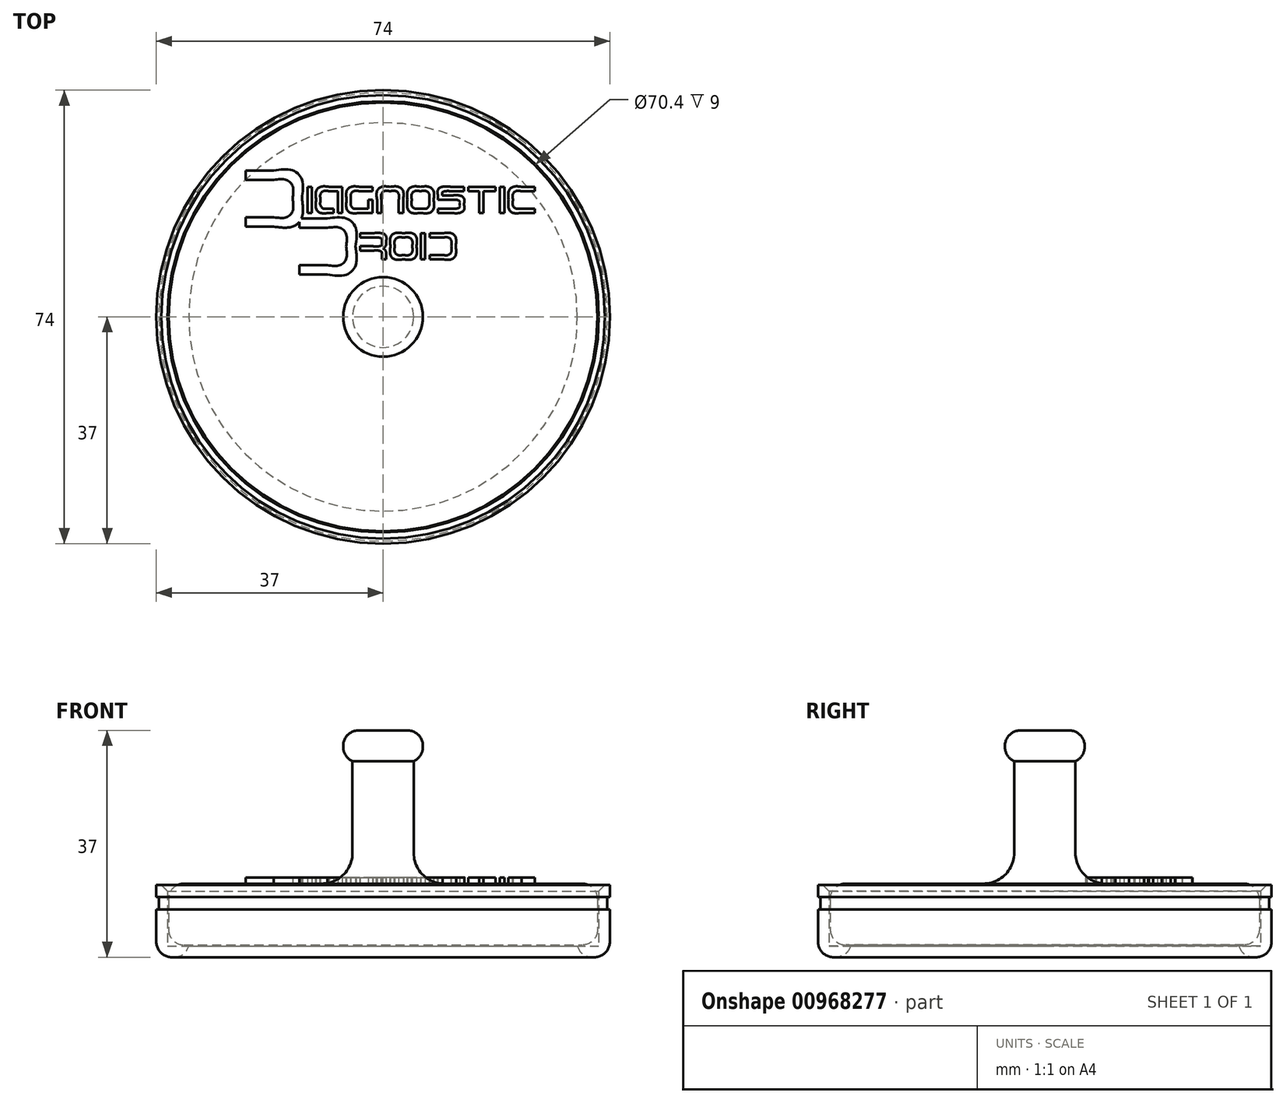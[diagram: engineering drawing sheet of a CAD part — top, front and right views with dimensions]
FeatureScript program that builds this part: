
annotation { "Feature Type Name" : "Feature", "Feature Type Description" : "" }
export const myFeature = defineFeature(function(context is Context, id is Id, definition is map)
    precondition{}
    {
        {
            var Q0;
            Q0=qCreatedBy(makeId("Front.planeOp"),FACE);
            var sketch = newSketch(context, id + "F0", { "sketchPlane" : qUnion([Q0])});
            skLineSegment(sketch, "E0.bottom", {"start": v(0, 0) * mm, "end": v(-35, 0) * mm});
            skLineSegment(sketch, "E0.top", {"start": v(0, 10) * mm, "end": v(-35, 10) * mm});
            skLineSegment(sketch, "E0.left", {"start": v(0, 0) * mm, "end": v(0, 10) * mm});
            skLineSegment(sketch, "E0.right", {"start": v(-35, 0) * mm, "end": v(-35, 6.5) * mm});
            skPoint(sketch, "E1.oppositeSnap0", {"position": v(-35, 5) * mm});
            skLineSegment(sketch, "E2.trimOffspring", {"start": v(-35, 3.5) * mm, "end": v(-35, 10) * mm});
            skLineSegment(sketch, "E3", {"start": v(-35, 6.5) * mm, "end": v(-35, 3.5) * mm});
            skPoint(sketch, "E1.top.end.orphan", {"position": v(-33.5, 6.5) * mm});
            skLineSegment(sketch, "E4.0", {"start": v(-37, -2) * mm, "end": v(-37, 9.8) * mm});
            skLineSegment(sketch, "E4.1", {"start": v(-31.7, -2) * mm, "end": v(-37, -2) * mm});
            skLineSegment(sketch, "E5.0", {"start": v(-35.2, -0.2) * mm, "end": v(-35.2, 9.8) * mm});
            skLineSegment(sketch, "E5.1", {"start": v(-31.7, -0.2) * mm, "end": v(-35.2, -0.2) * mm});
            skLineSegment(sketch, "E6", {"start": v(-35.2, 9.8) * mm, "end": v(-37, 9.8) * mm});
            skLineSegment(sketch, "E7", {"start": v(-31.7, -0.2) * mm, "end": v(-31.7, -2) * mm});
            skLineSegment(sketch, "E8.bottom", {"start": v(-37, 7.8) * mm, "end": v(-36.6, 7.8) * mm});
            skLineSegment(sketch, "E8.top", {"start": v(-37, 5.8) * mm, "end": v(-36.6, 5.8) * mm});
            skLineSegment(sketch, "E8.left", {"start": v(-37, 7.8) * mm, "end": v(-37, 5.8) * mm});
            skLineSegment(sketch, "E8.right", {"start": v(-36.6, 7.8) * mm, "end": v(-36.6, 5.8) * mm});
            skSolve(sketch);
        }
        {
            var Q0;
            Q0=makeQuery(id+"F0.imprint","IMPRINT",FACE,{"disambiguationData":[TD([[makeQuery(id+"F0.imprint","IMPRINT",EDGE,{"derivedFrom":sQuery(id+"F0.wireOp",EDGE,"E0.bottom")}),-1.0]])]});
            var Q1;
            Q1=makeQuery(id+"F0.imprint","IMPRINT",FACE,{"disambiguationData":[TD([[makeQuery(id+"F0.imprint","IMPRINT",EDGE,{"derivedFrom":sQuery(id+"F0.wireOp",EDGE,"E4.0")}),-1.0]])]});
            var Q2;
            Q2=sQuery(id+"F0.wireOp",EDGE,"E0.left");
            revolve(context, id + "F1", {"entities" : qUnion([Q0, Q1]), "axis" : qUnion([Q2]), "revolveType" : RevolveType.FULL});
        }
        {
            var Q0;
            Q0=makeQuery(id+"F1.opRevolve","SWEPT_FACE",FACE,{"disambiguationData":[OSD([sQuery(id+"F0.wireOp",EDGE,"E0.top")])]});
            var sketch = newSketch(context, id + "F2", { "sketchPlane" : qUnion([Q0])});
            skLineSegment(sketch, "E9", {"start": v(-11.63, 21.23) * mm, "end": v(-11.63, 16.97) * mm});
            skLineSegment(sketch, "E10", {"start": v(-11.63, 16.97) * mm, "end": v(-12.34, 16.97) * mm});
            skLineSegment(sketch, "E11", {"start": v(-12.34, 16.97) * mm, "end": v(-12.34, 21.23) * mm});
            skLineSegment(sketch, "E12", {"start": v(-12.34, 21.23) * mm, "end": v(-11.63, 21.23) * mm});
            skFitSpline(sketch, "E13", {"points": [v(-8.8, 20.52) * mm, v(-9.74, 20.52) * mm, v(-10.21, 20.04) * mm, v(-10.21, 19.1) * mm]});
            skFitSpline(sketch, "E14", {"points": [v(-10.21, 19.1) * mm, v(-10.21, 18.15) * mm, v(-9.74, 17.68) * mm, v(-8.8, 17.68) * mm]});
            skLineSegment(sketch, "E15", {"start": v(-6.67, 21.23) * mm, "end": v(-6.67, 16.97) * mm});
            skLineSegment(sketch, "E16", {"start": v(-6.67, 16.97) * mm, "end": v(-7.37, 16.97) * mm});
            skLineSegment(sketch, "E17", {"start": v(-7.37, 16.97) * mm, "end": v(-7.37, 20.52) * mm});
            skLineSegment(sketch, "E18", {"start": v(-7.37, 20.52) * mm, "end": v(-8.8, 20.52) * mm});
            skFitSpline(sketch, "E19", {"points": [v(-8.8, 16.97) * mm, v(-10.21, 16.97) * mm, v(-10.92, 17.68) * mm, v(-10.92, 19.1) * mm]});
            skFitSpline(sketch, "E20", {"points": [v(-10.92, 19.1) * mm, v(-10.92, 20.52) * mm, v(-10.21, 21.23) * mm, v(-8.8, 21.23) * mm]});
            skLineSegment(sketch, "E21", {"start": v(-8.8, 17.68) * mm, "end": v(-8.08, 17.68) * mm});
            skLineSegment(sketch, "E22", {"start": v(-8.08, 17.68) * mm, "end": v(-8.08, 16.97) * mm});
            skLineSegment(sketch, "E23", {"start": v(-8.08, 16.97) * mm, "end": v(-8.8, 16.97) * mm});
            skLineSegment(sketch, "E24", {"start": v(-8.8, 21.23) * mm, "end": v(-6.67, 21.23) * mm});
            skFitSpline(sketch, "E25", {"points": [v(-3.83, 16.97) * mm, v(-5.25, 16.97) * mm, v(-5.96, 17.68) * mm, v(-5.96, 19.1) * mm]});
            skFitSpline(sketch, "E26", {"points": [v(-5.96, 19.1) * mm, v(-5.96, 20.52) * mm, v(-5.25, 21.23) * mm, v(-3.83, 21.23) * mm]});
            skLineSegment(sketch, "E27", {"start": v(-1.7, 19.1) * mm, "end": v(-1.7, 16.97) * mm});
            skLineSegment(sketch, "E28", {"start": v(-1.7, 16.97) * mm, "end": v(-3.83, 16.97) * mm});
            skFitSpline(sketch, "E29", {"points": [v(-3.83, 20.52) * mm, v(-4.77, 20.52) * mm, v(-5.25, 20.04) * mm, v(-5.25, 19.1) * mm]});
            skFitSpline(sketch, "E30", {"points": [v(-5.25, 19.1) * mm, v(-5.25, 18.15) * mm, v(-4.77, 17.68) * mm, v(-3.83, 17.68) * mm]});
            skLineSegment(sketch, "E31", {"start": v(-3.83, 21.23) * mm, "end": v(-1.7, 21.23) * mm});
            skLineSegment(sketch, "E32", {"start": v(-1.7, 21.23) * mm, "end": v(-1.7, 20.52) * mm});
            skLineSegment(sketch, "E33", {"start": v(-1.7, 20.52) * mm, "end": v(-3.83, 20.52) * mm});
            skLineSegment(sketch, "E34", {"start": v(-3.83, 17.68) * mm, "end": v(-2.4, 17.68) * mm});
            skLineSegment(sketch, "E35", {"start": v(-2.4, 17.68) * mm, "end": v(-2.4, 19.1) * mm});
            skLineSegment(sketch, "E36", {"start": v(-2.4, 19.1) * mm, "end": v(-1.7, 19.1) * mm});
            skFitSpline(sketch, "E37", {"points": [v(-0.99, 19.1) * mm, v(-0.99, 20.52) * mm, v(-0.28, 21.23) * mm, v(1.14, 21.23) * mm]});
            skFitSpline(sketch, "E38", {"points": [v(1.14, 21.23) * mm, v(2.56, 21.23) * mm, v(3.27, 20.52) * mm, v(3.27, 19.1) * mm]});
            skLineSegment(sketch, "E39", {"start": v(-0.28, 19.1) * mm, "end": v(-0.28, 16.97) * mm});
            skLineSegment(sketch, "E40", {"start": v(-0.28, 16.97) * mm, "end": v(-0.99, 16.97) * mm});
            skLineSegment(sketch, "E41", {"start": v(-0.99, 16.97) * mm, "end": v(-0.99, 19.1) * mm});
            skFitSpline(sketch, "E42", {"points": [v(2.56, 19.1) * mm, v(2.56, 20.04) * mm, v(2.09, 20.52) * mm, v(1.14, 20.52) * mm]});
            skFitSpline(sketch, "E43", {"points": [v(1.14, 20.52) * mm, v(0.2, 20.52) * mm, v(-0.28, 20.04) * mm, v(-0.28, 19.1) * mm]});
            skLineSegment(sketch, "E44", {"start": v(3.27, 19.1) * mm, "end": v(3.27, 16.97) * mm});
            skLineSegment(sketch, "E45", {"start": v(3.27, 16.97) * mm, "end": v(2.56, 16.97) * mm});
            skLineSegment(sketch, "E46", {"start": v(2.56, 16.97) * mm, "end": v(2.56, 19.1) * mm});
            skFitSpline(sketch, "E47", {"points": [v(3.98, 19.1) * mm, v(3.98, 20.52) * mm, v(4.7, 21.23) * mm, v(6.11, 21.23) * mm]});
            skFitSpline(sketch, "E48", {"points": [v(6.11, 21.23) * mm, v(7.53, 21.23) * mm, v(8.24, 20.52) * mm, v(8.24, 19.1) * mm]});
            skFitSpline(sketch, "E49", {"points": [v(8.24, 19.1) * mm, v(8.24, 17.68) * mm, v(7.53, 16.97) * mm, v(6.11, 16.97) * mm]});
            skFitSpline(sketch, "E50", {"points": [v(6.11, 16.97) * mm, v(4.7, 16.97) * mm, v(3.98, 17.68) * mm, v(3.98, 19.1) * mm]});
            skFitSpline(sketch, "E51", {"points": [v(4.7, 19.1) * mm, v(4.7, 18.15) * mm, v(5.16, 17.68) * mm, v(6.11, 17.68) * mm]});
            skFitSpline(sketch, "E52", {"points": [v(6.11, 17.68) * mm, v(7.06, 17.68) * mm, v(7.53, 18.15) * mm, v(7.53, 19.1) * mm]});
            skFitSpline(sketch, "E53", {"points": [v(7.53, 19.1) * mm, v(7.53, 20.04) * mm, v(7.06, 20.52) * mm, v(6.11, 20.52) * mm]});
            skFitSpline(sketch, "E54", {"points": [v(6.11, 20.52) * mm, v(5.16, 20.52) * mm, v(4.7, 20.04) * mm, v(4.7, 19.1) * mm]});
            skFitSpline(sketch, "E55", {"points": [v(8.95, 19.8) * mm, v(8.95, 20.75) * mm, v(9.66, 21.23) * mm, v(11.08, 21.23) * mm]});
            skFitSpline(sketch, "E56", {"points": [v(11.08, 20.52) * mm, v(10.13, 20.52) * mm, v(9.66, 20.28) * mm, v(9.66, 19.8) * mm]});
            skLineSegment(sketch, "E57", {"start": v(11.08, 21.23) * mm, "end": v(13.2, 21.23) * mm});
            skLineSegment(sketch, "E58", {"start": v(13.2, 21.23) * mm, "end": v(13.2, 20.52) * mm});
            skLineSegment(sketch, "E59", {"start": v(13.2, 20.52) * mm, "end": v(11.08, 20.52) * mm});
            skFitSpline(sketch, "E60", {"points": [v(11.08, 19.8) * mm, v(12.5, 19.8) * mm, v(13.2, 19.33) * mm, v(13.2, 18.39) * mm]});
            skFitSpline(sketch, "E61", {"points": [v(13.2, 18.39) * mm, v(13.2, 17.44) * mm, v(12.5, 16.97) * mm, v(11.08, 16.97) * mm]});
            skLineSegment(sketch, "E62", {"start": v(9.66, 19.8) * mm, "end": v(11.08, 19.8) * mm});
            skFitSpline(sketch, "E63", {"points": [v(11.08, 17.68) * mm, v(12.03, 17.68) * mm, v(12.5, 17.91) * mm, v(12.5, 18.39) * mm]});
            skFitSpline(sketch, "E64", {"points": [v(12.5, 18.39) * mm, v(12.5, 18.86) * mm, v(12.03, 19.1) * mm, v(11.08, 19.1) * mm]});
            skLineSegment(sketch, "E65", {"start": v(11.08, 16.97) * mm, "end": v(8.95, 16.97) * mm});
            skLineSegment(sketch, "E66", {"start": v(8.95, 16.97) * mm, "end": v(8.95, 17.68) * mm});
            skLineSegment(sketch, "E67", {"start": v(8.95, 17.68) * mm, "end": v(11.08, 17.68) * mm});
            skLineSegment(sketch, "E68", {"start": v(11.08, 19.1) * mm, "end": v(8.95, 19.1) * mm});
            skLineSegment(sketch, "E69", {"start": v(8.95, 19.1) * mm, "end": v(8.95, 19.8) * mm});
            skLineSegment(sketch, "E70", {"start": v(13.92, 21.23) * mm, "end": v(18.36, 21.23) * mm});
            skLineSegment(sketch, "E71", {"start": v(18.36, 21.23) * mm, "end": v(18.36, 20.52) * mm});
            skLineSegment(sketch, "E72", {"start": v(18.36, 20.52) * mm, "end": v(16.4, 20.52) * mm});
            skLineSegment(sketch, "E73", {"start": v(16.4, 20.52) * mm, "end": v(16.4, 16.97) * mm});
            skLineSegment(sketch, "E74", {"start": v(16.4, 16.97) * mm, "end": v(15.7, 16.97) * mm});
            skLineSegment(sketch, "E75", {"start": v(15.7, 16.97) * mm, "end": v(15.7, 20.52) * mm});
            skLineSegment(sketch, "E76", {"start": v(15.7, 20.52) * mm, "end": v(13.92, 20.52) * mm});
            skLineSegment(sketch, "E77", {"start": v(13.92, 20.52) * mm, "end": v(13.92, 21.23) * mm});
            skFitSpline(sketch, "E78", {"points": [v(21.2, 19.1) * mm, v(21.2, 18.15) * mm, v(21.67, 17.68) * mm, v(22.62, 17.68) * mm]});
            skLineSegment(sketch, "E79", {"start": v(19.78, 21.23) * mm, "end": v(19.78, 16.97) * mm});
            skLineSegment(sketch, "E80", {"start": v(19.78, 16.97) * mm, "end": v(19.07, 16.97) * mm});
            skLineSegment(sketch, "E81", {"start": v(19.07, 16.97) * mm, "end": v(19.07, 21.23) * mm});
            skLineSegment(sketch, "E82", {"start": v(19.07, 21.23) * mm, "end": v(19.78, 21.23) * mm});
            skFitSpline(sketch, "E83", {"points": [v(22.62, 16.97) * mm, v(21.2, 16.97) * mm, v(20.5, 17.68) * mm, v(20.5, 19.1) * mm]});
            skFitSpline(sketch, "E84", {"points": [v(20.5, 19.1) * mm, v(20.5, 20.52) * mm, v(21.2, 21.23) * mm, v(22.62, 21.23) * mm]});
            skLineSegment(sketch, "E85", {"start": v(22.62, 17.68) * mm, "end": v(24.75, 17.68) * mm});
            skLineSegment(sketch, "E86", {"start": v(24.75, 17.68) * mm, "end": v(24.75, 16.97) * mm});
            skLineSegment(sketch, "E87", {"start": v(24.75, 16.97) * mm, "end": v(22.62, 16.97) * mm});
            skFitSpline(sketch, "E88", {"points": [v(22.62, 20.52) * mm, v(21.67, 20.52) * mm, v(21.2, 20.04) * mm, v(21.2, 19.1) * mm]});
            skLineSegment(sketch, "E89", {"start": v(22.62, 21.23) * mm, "end": v(24.75, 21.23) * mm});
            skLineSegment(sketch, "E90", {"start": v(24.75, 21.23) * mm, "end": v(24.75, 20.52) * mm});
            skLineSegment(sketch, "E91", {"start": v(24.75, 20.52) * mm, "end": v(22.62, 20.52) * mm});
            skFitSpline(sketch, "E92", {"points": [v(-1.64, 11.52) * mm, v(-0.7, 11.52) * mm, v(-0.22, 11.76) * mm, v(-0.22, 12.23) * mm]});
            skFitSpline(sketch, "E93", {"points": [v(-0.22, 12.23) * mm, v(-0.22, 12.7) * mm, v(-0.7, 12.94) * mm, v(-1.64, 12.94) * mm]});
            skFitSpline(sketch, "E94", {"points": [v(-1.64, 13.65) * mm, v(-0.22, 13.65) * mm, v(0.5, 13.18) * mm, v(0.5, 12.23) * mm]});
            skFitSpline(sketch, "E95", {"points": [v(0.5, 12.23) * mm, v(0.5, 11.76) * mm, v(0.32, 11.4) * mm, v(-0.04, 11.17) * mm]});
            skFitSpline(sketch, "E96", {"points": [v(-0.04, 11.17) * mm, v(0.32, 10.93) * mm, v(0.5, 10.58) * mm, v(0.5, 10.1) * mm]});
            skLineSegment(sketch, "E97", {"start": v(-1.64, 12.94) * mm, "end": v(-3.77, 12.94) * mm});
            skLineSegment(sketch, "E98", {"start": v(-3.77, 12.94) * mm, "end": v(-3.77, 13.65) * mm});
            skLineSegment(sketch, "E99", {"start": v(-3.77, 13.65) * mm, "end": v(-1.64, 13.65) * mm});
            skFitSpline(sketch, "E100", {"points": [v(-0.22, 10.1) * mm, v(-0.22, 10.58) * mm, v(-0.7, 10.81) * mm, v(-1.64, 10.81) * mm]});
            skLineSegment(sketch, "E101", {"start": v(0.5, 10.1) * mm, "end": v(0.5, 9.4) * mm});
            skLineSegment(sketch, "E102", {"start": v(0.5, 9.4) * mm, "end": v(-0.22, 9.4) * mm});
            skLineSegment(sketch, "E103", {"start": v(-0.22, 9.4) * mm, "end": v(-0.22, 10.1) * mm});
            skFitSpline(sketch, "E104", {"points": [v(1.2, 11.52) * mm, v(1.2, 12.94) * mm, v(1.91, 13.65) * mm, v(3.33, 13.65) * mm]});
            skFitSpline(sketch, "E105", {"points": [v(3.33, 13.65) * mm, v(4.75, 13.65) * mm, v(5.46, 12.94) * mm, v(5.46, 11.52) * mm]});
            skFitSpline(sketch, "E106", {"points": [v(5.46, 11.52) * mm, v(5.46, 10.1) * mm, v(4.75, 9.4) * mm, v(3.33, 9.4) * mm]});
            skFitSpline(sketch, "E107", {"points": [v(3.33, 9.4) * mm, v(1.91, 9.4) * mm, v(1.2, 10.1) * mm, v(1.2, 11.52) * mm]});
            skLineSegment(sketch, "E108", {"start": v(-1.64, 10.81) * mm, "end": v(-3.77, 10.81) * mm});
            skLineSegment(sketch, "E109", {"start": v(-3.77, 10.81) * mm, "end": v(-3.77, 11.52) * mm});
            skLineSegment(sketch, "E110", {"start": v(-3.77, 11.52) * mm, "end": v(-1.64, 11.52) * mm});
            skFitSpline(sketch, "E111", {"points": [v(1.91, 11.52) * mm, v(1.91, 10.58) * mm, v(2.39, 10.1) * mm, v(3.33, 10.1) * mm]});
            skFitSpline(sketch, "E112", {"points": [v(3.33, 10.1) * mm, v(4.28, 10.1) * mm, v(4.75, 10.58) * mm, v(4.75, 11.52) * mm]});
            skFitSpline(sketch, "E113", {"points": [v(4.75, 11.52) * mm, v(4.75, 12.47) * mm, v(4.28, 12.94) * mm, v(3.33, 12.94) * mm]});
            skFitSpline(sketch, "E114", {"points": [v(3.33, 12.94) * mm, v(2.39, 12.94) * mm, v(1.91, 12.47) * mm, v(1.91, 11.52) * mm]});
            skLineSegment(sketch, "E115", {"start": v(6.88, 13.65) * mm, "end": v(6.88, 9.4) * mm});
            skLineSegment(sketch, "E116", {"start": v(6.88, 9.4) * mm, "end": v(6.17, 9.4) * mm});
            skLineSegment(sketch, "E117", {"start": v(6.17, 9.4) * mm, "end": v(6.17, 13.65) * mm});
            skLineSegment(sketch, "E118", {"start": v(6.17, 13.65) * mm, "end": v(6.88, 13.65) * mm});
            skFitSpline(sketch, "E119", {"points": [v(9.72, 13.65) * mm, v(11.14, 13.65) * mm, v(11.85, 12.94) * mm, v(11.85, 11.52) * mm]});
            skFitSpline(sketch, "E120", {"points": [v(11.85, 11.52) * mm, v(11.85, 10.1) * mm, v(11.14, 9.4) * mm, v(9.72, 9.4) * mm]});
            skLineSegment(sketch, "E121", {"start": v(9.72, 12.94) * mm, "end": v(7.6, 12.94) * mm});
            skLineSegment(sketch, "E122", {"start": v(7.6, 12.94) * mm, "end": v(7.6, 13.65) * mm});
            skLineSegment(sketch, "E123", {"start": v(7.6, 13.65) * mm, "end": v(9.72, 13.65) * mm});
            skFitSpline(sketch, "E124", {"points": [v(9.72, 10.1) * mm, v(10.67, 10.1) * mm, v(11.14, 10.58) * mm, v(11.14, 11.52) * mm]});
            skFitSpline(sketch, "E125", {"points": [v(11.14, 11.52) * mm, v(11.14, 12.47) * mm, v(10.67, 12.94) * mm, v(9.72, 12.94) * mm]});
            skLineSegment(sketch, "E126", {"start": v(9.72, 9.4) * mm, "end": v(7.6, 9.4) * mm});
            skLineSegment(sketch, "E127", {"start": v(7.6, 9.4) * mm, "end": v(7.6, 10.1) * mm});
            skLineSegment(sketch, "E128", {"start": v(7.6, 10.1) * mm, "end": v(9.72, 10.1) * mm});
            skFitSpline(sketch, "E129", {"points": [v(-17.82, 23.9) * mm, v(-14.77, 23.9) * mm, v(-13.24, 22.37) * mm, v(-13.24, 19.3) * mm]});
            skFitSpline(sketch, "E130", {"points": [v(-13.24, 19.3) * mm, v(-13.24, 16.25) * mm, v(-14.77, 14.72) * mm, v(-17.82, 14.72) * mm]});
            skLineSegment(sketch, "E131", {"start": v(-17.82, 22.37) * mm, "end": v(-22.4, 22.37) * mm});
            skLineSegment(sketch, "E132", {"start": v(-22.4, 22.37) * mm, "end": v(-22.4, 23.9) * mm});
            skLineSegment(sketch, "E133", {"start": v(-22.4, 23.9) * mm, "end": v(-17.82, 23.9) * mm});
            skFitSpline(sketch, "E134", {"points": [v(-17.82, 16.25) * mm, v(-15.79, 16.25) * mm, v(-14.77, 17.27) * mm, v(-14.77, 19.3) * mm]});
            skFitSpline(sketch, "E135", {"points": [v(-14.77, 19.3) * mm, v(-14.77, 21.35) * mm, v(-15.79, 22.37) * mm, v(-17.82, 22.37) * mm]});
            skLineSegment(sketch, "E136", {"start": v(-17.82, 14.72) * mm, "end": v(-22.4, 14.72) * mm});
            skLineSegment(sketch, "E137", {"start": v(-22.4, 14.72) * mm, "end": v(-22.4, 16.25) * mm});
            skLineSegment(sketch, "E138", {"start": v(-22.4, 16.25) * mm, "end": v(-17.82, 16.25) * mm});
            skFitSpline(sketch, "E139", {"points": [v(-9.08, 16.07) * mm, v(-6.02, 16.07) * mm, v(-4.5, 14.54) * mm, v(-4.5, 11.48) * mm]});
            skFitSpline(sketch, "E140", {"points": [v(-4.5, 11.48) * mm, v(-4.5, 8.42) * mm, v(-6.02, 6.9) * mm, v(-9.08, 6.9) * mm]});
            skLineSegment(sketch, "E141", {"start": v(-9.08, 14.54) * mm, "end": v(-13.66, 14.54) * mm});
            skLineSegment(sketch, "E142", {"start": v(-13.66, 14.54) * mm, "end": v(-13.66, 16.07) * mm});
            skLineSegment(sketch, "E143", {"start": v(-13.66, 16.07) * mm, "end": v(-9.08, 16.07) * mm});
            skFitSpline(sketch, "E144", {"points": [v(-9.08, 8.42) * mm, v(-7.04, 8.42) * mm, v(-6.02, 9.44) * mm, v(-6.02, 11.48) * mm]});
            skFitSpline(sketch, "E145", {"points": [v(-6.02, 11.48) * mm, v(-6.02, 13.52) * mm, v(-7.04, 14.54) * mm, v(-9.08, 14.54) * mm]});
            skLineSegment(sketch, "E146", {"start": v(-9.04, 6.9) * mm, "end": v(-13.66, 6.9) * mm});
            skLineSegment(sketch, "E147", {"start": v(-13.66, 8.42) * mm, "end": v(-9.04, 8.42) * mm});
            skLineSegment(sketch, "E148", {"start": v(-13.66, 8.42) * mm, "end": v(-13.66, 6.9) * mm});
            skSolve(sketch);
        }
        {
            var Q0;
            Q0=makeQuery(id+"F2.imprint","IMPRINT",FACE,{"disambiguationData":[TD([[makeQuery(id+"F2.imprint","IMPRINT",EDGE,{"derivedFrom":sQuery(id+"F2.wireOp",EDGE,"E139")}),-1.0]])]});
            var Q1;
            Q1=makeQuery(id+"F2.imprint","IMPRINT",FACE,{"disambiguationData":[TD([[makeQuery(id+"F2.imprint","IMPRINT",EDGE,{"derivedFrom":sQuery(id+"F2.wireOp",EDGE,"E92")}),-1.0]])]});
            var Q2;
            Q2=makeQuery(id+"F2.imprint","IMPRINT",FACE,{"disambiguationData":[TD([[makeQuery(id+"F2.imprint","IMPRINT",EDGE,{"derivedFrom":sQuery(id+"F2.wireOp",EDGE,"E104")}),-1.0]])]});
            var Q3;
            Q3=makeQuery(id+"F2.imprint","IMPRINT",FACE,{"disambiguationData":[TD([[makeQuery(id+"F2.imprint","IMPRINT",EDGE,{"derivedFrom":sQuery(id+"F2.wireOp",EDGE,"E119")}),-1.0]])]});
            var Q4;
            Q4=makeQuery(id+"F2.imprint","IMPRINT",FACE,{"disambiguationData":[TD([[makeQuery(id+"F2.imprint","IMPRINT",EDGE,{"derivedFrom":sQuery(id+"F2.wireOp",EDGE,"E115")}),-1.0]])]});
            var Q5;
            Q5=makeQuery(id+"F2.imprint","IMPRINT",FACE,{"disambiguationData":[TD([[makeQuery(id+"F2.imprint","IMPRINT",EDGE,{"derivedFrom":sQuery(id+"F2.wireOp",EDGE,"E37")}),-1.0]])]});
            var Q6;
            Q6=makeQuery(id+"F2.imprint","IMPRINT",FACE,{"disambiguationData":[TD([[makeQuery(id+"F2.imprint","IMPRINT",EDGE,{"derivedFrom":sQuery(id+"F2.wireOp",EDGE,"E25")}),-1.0]])]});
            var Q7;
            Q7=makeQuery(id+"F2.imprint","IMPRINT",FACE,{"disambiguationData":[TD([[makeQuery(id+"F2.imprint","IMPRINT",EDGE,{"derivedFrom":sQuery(id+"F2.wireOp",EDGE,"E13")}),-1.0]])]});
            var Q8;
            Q8=makeQuery(id+"F2.imprint","IMPRINT",FACE,{"disambiguationData":[TD([[makeQuery(id+"F2.imprint","IMPRINT",EDGE,{"derivedFrom":sQuery(id+"F2.wireOp",EDGE,"E9")}),-1.0]])]});
            var Q9;
            Q9=makeQuery(id+"F2.imprint","IMPRINT",FACE,{"disambiguationData":[TD([[makeQuery(id+"F2.imprint","IMPRINT",EDGE,{"derivedFrom":sQuery(id+"F2.wireOp",EDGE,"E129")}),-1.0]])]});
            var Q10;
            Q10=makeQuery(id+"F2.imprint","IMPRINT",FACE,{"disambiguationData":[TD([[makeQuery(id+"F2.imprint","IMPRINT",EDGE,{"derivedFrom":sQuery(id+"F2.wireOp",EDGE,"E47")}),-1.0]])]});
            var Q11;
            Q11=makeQuery(id+"F2.imprint","IMPRINT",FACE,{"disambiguationData":[TD([[makeQuery(id+"F2.imprint","IMPRINT",EDGE,{"derivedFrom":sQuery(id+"F2.wireOp",EDGE,"E55")}),-1.0]])]});
            var Q12;
            Q12=makeQuery(id+"F2.imprint","IMPRINT",FACE,{"disambiguationData":[TD([[makeQuery(id+"F2.imprint","IMPRINT",EDGE,{"derivedFrom":sQuery(id+"F2.wireOp",EDGE,"E70")}),-1.0]])]});
            var Q13;
            Q13=makeQuery(id+"F2.imprint","IMPRINT",FACE,{"disambiguationData":[TD([[makeQuery(id+"F2.imprint","IMPRINT",EDGE,{"derivedFrom":sQuery(id+"F2.wireOp",EDGE,"E79")}),-1.0]])]});
            var Q14;
            Q14=makeQuery(id+"F2.imprint","IMPRINT",FACE,{"disambiguationData":[TD([[makeQuery(id+"F2.imprint","IMPRINT",EDGE,{"derivedFrom":sQuery(id+"F2.wireOp",EDGE,"E78")}),-1.0]])]});
            var Q15;
            Q15=sQuery(id+"F2.wireOp",EDGE,"E99");
            var Q16;
            Q16=sQuery(id+"F2.wireOp",EDGE,"E115");
            var Q17;
            Q17=sQuery(id+"F2.wireOp",EDGE,"E131");
            var Q18;
            Q18=sQuery(id+"F2.wireOp",EDGE,"E147");
            var Q19;
            Q19=sQuery(id+"F2.wireOp",EDGE,"E51");
            var Q20;
            Q20=sQuery(id+"F2.wireOp",EDGE,"E67");
            var Q21;
            Q21=sQuery(id+"F2.wireOp",EDGE,"E83");
            var Q22;
            Q22=sQuery(id+"F2.wireOp",EDGE,"E114");
            var Q23;
            Q23=sQuery(id+"F2.wireOp",EDGE,"E130");
            var Q24;
            Q24=sQuery(id+"F2.wireOp",EDGE,"E146");
            var Q25;
            Q25=sQuery(id+"F2.wireOp",EDGE,"E50");
            var Q26;
            Q26=sQuery(id+"F2.wireOp",EDGE,"E20");
            var Q27;
            Q27=sQuery(id+"F2.wireOp",EDGE,"E19");
            var Q28;
            Q28=sQuery(id+"F2.wireOp",EDGE,"E17");
            var Q29;
            Q29=sQuery(id+"F2.wireOp",EDGE,"E15");
            var Q30;
            Q30=sQuery(id+"F2.wireOp",EDGE,"E14");
            var Q31;
            Q31=sQuery(id+"F2.wireOp",EDGE,"E13");
            var Q32;
            Q32=sQuery(id+"F2.wireOp",EDGE,"E11");
            var Q33;
            Q33=sQuery(id+"F2.wireOp",EDGE,"E9");
            var Q34;
            Q34=sQuery(id+"F2.wireOp",EDGE,"E97");
            var Q35;
            Q35=sQuery(id+"F2.wireOp",EDGE,"E113");
            var Q36;
            Q36=sQuery(id+"F2.wireOp",EDGE,"E129");
            var Q37;
            Q37=sQuery(id+"F2.wireOp",EDGE,"E145");
            var Q38;
            Q38=sQuery(id+"F2.wireOp",EDGE,"E33");
            var Q39;
            Q39=sQuery(id+"F2.wireOp",EDGE,"E49");
            var Q40;
            Q40=sQuery(id+"F2.wireOp",EDGE,"E65");
            var Q41;
            Q41=sQuery(id+"F2.wireOp",EDGE,"E81");
            var Q42;
            Q42=sQuery(id+"F2.wireOp",EDGE,"E112");
            var Q43;
            Q43=sQuery(id+"F2.wireOp",EDGE,"E128");
            var Q44;
            Q44=sQuery(id+"F2.wireOp",EDGE,"E144");
            var Q45;
            Q45=sQuery(id+"F2.wireOp",EDGE,"E48");
            var Q46;
            Q46=sQuery(id+"F2.wireOp",EDGE,"E143");
            var Q47;
            Q47=sQuery(id+"F2.wireOp",EDGE,"E79");
            var Q48;
            Q48=sQuery(id+"F2.wireOp",EDGE,"E111");
            var Q49;
            Q49=sQuery(id+"F2.wireOp",EDGE,"E31");
            var Q50;
            Q50=sQuery(id+"F2.wireOp",EDGE,"E47");
            var Q51;
            Q51=sQuery(id+"F2.wireOp",EDGE,"E126");
            var Q52;
            Q52=sQuery(id+"F2.wireOp",EDGE,"E78");
            var Q53;
            Q53=sQuery(id+"F2.wireOp",EDGE,"E94");
            var Q54;
            Q54=sQuery(id+"F2.wireOp",EDGE,"E110");
            var Q55;
            Q55=sQuery(id+"F2.wireOp",EDGE,"E125");
            var Q56;
            Q56=sQuery(id+"F2.wireOp",EDGE,"E141");
            var Q57;
            Q57=sQuery(id+"F2.wireOp",EDGE,"E61");
            var Q58;
            Q58=sQuery(id+"F2.wireOp",EDGE,"E29");
            var Q59;
            Q59=sQuery(id+"F2.wireOp",EDGE,"E124");
            var Q60;
            Q60=sQuery(id+"F2.wireOp",EDGE,"E140");
            var Q61;
            Q61=sQuery(id+"F2.wireOp",EDGE,"E60");
            var Q62;
            Q62=sQuery(id+"F2.wireOp",EDGE,"E108");
            var Q63;
            Q63=sQuery(id+"F2.wireOp",EDGE,"E123");
            var Q64;
            Q64=sQuery(id+"F2.wireOp",EDGE,"E139");
            var Q65;
            Q65=sQuery(id+"F2.wireOp",EDGE,"E59");
            var Q66;
            Q66=sQuery(id+"F2.wireOp",EDGE,"E75");
            var Q67;
            Q67=sQuery(id+"F2.wireOp",EDGE,"E91");
            var Q68;
            Q68=sQuery(id+"F2.wireOp",EDGE,"E107");
            var Q69;
            Q69=sQuery(id+"F2.wireOp",EDGE,"E43");
            var Q70;
            Q70=sQuery(id+"F2.wireOp",EDGE,"E106");
            var Q71;
            Q71=sQuery(id+"F2.wireOp",EDGE,"E26");
            var Q72;
            Q72=sQuery(id+"F2.wireOp",EDGE,"E42");
            var Q73;
            Q73=sQuery(id+"F2.wireOp",EDGE,"E138");
            var Q74;
            Q74=sQuery(id+"F2.wireOp",EDGE,"E25");
            var Q75;
            Q75=sQuery(id+"F2.wireOp",EDGE,"E121");
            var Q76;
            Q76=sQuery(id+"F2.wireOp",EDGE,"E57");
            var Q77;
            Q77=sQuery(id+"F2.wireOp",EDGE,"E73");
            var Q78;
            Q78=sQuery(id+"F2.wireOp",EDGE,"E89");
            var Q79;
            Q79=sQuery(id+"F2.wireOp",EDGE,"E105");
            var Q80;
            Q80=sQuery(id+"F2.wireOp",EDGE,"E120");
            var Q81;
            Q81=sQuery(id+"F2.wireOp",EDGE,"E88");
            var Q82;
            Q82=sQuery(id+"F2.wireOp",EDGE,"E104");
            var Q83;
            Q83=sQuery(id+"F2.wireOp",EDGE,"E119");
            var Q84;
            Q84=sQuery(id+"F2.wireOp",EDGE,"E135");
            var Q85;
            Q85=sQuery(id+"F2.wireOp",EDGE,"E55");
            var Q86;
            Q86=sQuery(id+"F2.wireOp",EDGE,"E87");
            var Q87;
            Q87=sQuery(id+"F2.wireOp",EDGE,"E117");
            var Q88;
            Q88=sQuery(id+"F2.wireOp",EDGE,"E133");
            var Q89;
            Q89=sQuery(id+"F2.wireOp",EDGE,"E37");
            var Q90;
            Q90=sQuery(id+"F2.wireOp",EDGE,"E53");
            var Q91;
            Q91=sQuery(id+"F2.wireOp",EDGE,"E85");
            var Q92;
            Q92=sQuery(id+"F2.wireOp",EDGE,"E134");
            var Q93;
            Q93=sQuery(id+"F2.wireOp",EDGE,"E54");
            var Q94;
            Q94=sQuery(id+"F2.wireOp",EDGE,"E38");
            var Q95;
            Q95=sQuery(id+"F2.wireOp",EDGE,"E52");
            var Q96;
            Q96=sQuery(id+"F2.wireOp",EDGE,"E68");
            var Q97;
            Q97=sQuery(id+"F2.wireOp",EDGE,"E84");
            var Q98;
            Q98=sQuery(id+"F2.wireOp",EDGE,"E35");
            var Q99;
            Q99=sQuery(id+"F2.wireOp",EDGE,"E34");
            var Q100;
            Q100=sQuery(id+"F2.wireOp",EDGE,"E66");
            var Q101;
            Q101=sQuery(id+"F2.wireOp",EDGE,"E82");
            var Q102;
            Q102=sQuery(id+"F2.wireOp",EDGE,"E18");
            var Q103;
            Q103=sQuery(id+"F2.wireOp",EDGE,"E12");
            var Q104;
            Q104=sQuery(id+"F2.wireOp",EDGE,"E10");
            var Q105;
            Q105=sQuery(id+"F2.wireOp",EDGE,"E24");
            var Q106;
            Q106=sQuery(id+"F2.wireOp",EDGE,"E96");
            var Q107;
            Q107=sQuery(id+"F2.wireOp",EDGE,"E32");
            var Q108;
            Q108=sQuery(id+"F2.wireOp",EDGE,"E64");
            var Q109;
            Q109=sQuery(id+"F2.wireOp",EDGE,"E80");
            var Q110;
            Q110=sQuery(id+"F2.wireOp",EDGE,"E127");
            var Q111;
            Q111=sQuery(id+"F2.wireOp",EDGE,"E63");
            var Q112;
            Q112=sQuery(id+"F2.wireOp",EDGE,"E95");
            var Q113;
            Q113=sQuery(id+"F2.wireOp",EDGE,"E142");
            var Q114;
            Q114=sQuery(id+"F2.wireOp",EDGE,"E62");
            var Q115;
            Q115=sQuery(id+"F2.wireOp",EDGE,"E30");
            var Q116;
            Q116=sQuery(id+"F2.wireOp",EDGE,"E46");
            var Q117;
            Q117=sQuery(id+"F2.wireOp",EDGE,"E77");
            var Q118;
            Q118=sQuery(id+"F2.wireOp",EDGE,"E93");
            var Q119;
            Q119=sQuery(id+"F2.wireOp",EDGE,"E109");
            var Q120;
            Q120=sQuery(id+"F2.wireOp",EDGE,"E45");
            var Q121;
            Q121=sQuery(id+"F2.wireOp",EDGE,"E76");
            var Q122;
            Q122=sQuery(id+"F2.wireOp",EDGE,"E92");
            var Q123;
            Q123=sQuery(id+"F2.wireOp",EDGE,"E28");
            var Q124;
            Q124=sQuery(id+"F2.wireOp",EDGE,"E44");
            var Q125;
            Q125=sQuery(id+"F2.wireOp",EDGE,"E27");
            var Q126;
            Q126=sQuery(id+"F2.wireOp",EDGE,"E58");
            var Q127;
            Q127=sQuery(id+"F2.wireOp",EDGE,"E74");
            var Q128;
            Q128=sQuery(id+"F2.wireOp",EDGE,"E90");
            var Q129;
            Q129=sQuery(id+"F2.wireOp",EDGE,"E41");
            var Q130;
            Q130=sQuery(id+"F2.wireOp",EDGE,"E137");
            var Q131;
            Q131=sQuery(id+"F2.wireOp",EDGE,"E56");
            var Q132;
            Q132=sQuery(id+"F2.wireOp",EDGE,"E72");
            var Q133;
            Q133=sQuery(id+"F2.wireOp",EDGE,"E71");
            var Q134;
            Q134=sQuery(id+"F2.wireOp",EDGE,"E103");
            var Q135;
            Q135=sQuery(id+"F2.wireOp",EDGE,"E39");
            var Q136;
            Q136=sQuery(id+"F2.wireOp",EDGE,"E101");
            var Q137;
            Q137=sQuery(id+"F2.wireOp",EDGE,"E70");
            var Q138;
            Q138=sQuery(id+"F2.wireOp",EDGE,"E86");
            var Q139;
            Q139=sQuery(id+"F2.wireOp",EDGE,"E102");
            var Q140;
            Q140=sQuery(id+"F2.wireOp",EDGE,"E100");
            var Q141;
            Q141=sQuery(id+"F2.wireOp",EDGE,"E116");
            var Q142;
            Q142=sQuery(id+"F2.wireOp",EDGE,"E132");
            var Q143;
            Q143=sQuery(id+"F2.wireOp",EDGE,"E148");
            var Q144;
            Q144=sQuery(id+"F2.wireOp",EDGE,"E36");
            var Q145;
            Q145=sQuery(id+"F2.wireOp",EDGE,"E16");
            var Q146;
            Q146=sQuery(id+"F2.wireOp",EDGE,"E122");
            var Q147;
            Q147=sQuery(id+"F2.wireOp",EDGE,"E40");
            var Q148;
            Q148=sQuery(id+"F2.wireOp",EDGE,"E118");
            var Q149;
            Q149=sQuery(id+"F2.wireOp",EDGE,"E98");
            var Q150;
            Q150=sQuery(id+"F2.wireOp",EDGE,"E21");
            var Q151;
            Q151=sQuery(id+"F2.wireOp",EDGE,"E23");
            var Q152;
            Q152=sQuery(id+"F2.wireOp",EDGE,"E22");
            var Q153;
            Q153=sQuery(id+"F2.wireOp",EDGE,"E69");
            var Q154;
            Q154=sQuery(id+"F2.wireOp",EDGE,"E136");
            extrude(context, id + "F3", {"entities" : qUnion([Q0, Q1, Q2, Q3, Q4, Q5, Q6, Q7, Q8, Q9, Q10, Q11, Q12, Q13, Q14]), "operationType" : NewBodyOperationType.REMOVE, "surfaceEntities" : qUnion([Q15, Q16, Q17, Q18, Q19, Q20, Q21, Q22, Q23, Q24, Q25, Q26, Q27, Q28, Q29, Q30, Q31, Q32, Q33, Q34, Q35, Q36, Q37, Q38, Q39, Q40, Q41, Q42, Q43, Q44, Q45, Q46, Q47, Q48, Q49, Q50, Q51, Q52, Q53, Q54, Q55, Q56, Q57, Q58, Q59, Q60, Q61, Q62, Q63, Q64, Q65, Q66, Q67, Q68, Q69, Q70, Q71, Q72, Q73, Q74, Q75, Q76, Q77, Q78, Q79, Q80, Q81, Q82, Q83, Q84, Q85, Q86, Q87, Q88, Q89, Q90, Q91, Q92, Q93, Q94, Q95, Q96, Q97, Q98, Q99, Q100, Q101, Q102, Q103, Q104, Q105, Q106, Q107, Q108, Q109, Q110, Q111, Q112, Q113, Q114, Q115, Q116, Q117, Q118, Q119, Q120, Q121, Q122, Q123, Q124, Q125, Q126, Q127, Q128, Q129, Q130, Q131, Q132, Q133, Q134, Q135, Q136, Q137, Q138, Q139, Q140, Q141, Q142, Q143, Q144, Q145, Q146, Q147, Q148, Q149, Q150, Q151, Q152, Q153, Q154]), "depth" : 1 * mm, "offsetDistance" : 25 * mm});
        }
        {
            var Q0;
            Q0=qSketchRegion(id+"F2",true);
            extrude(context, id + "F4", {"entities" : qUnion([Q0]), "operationType" : NewBodyOperationType.ADD, "depth" : 1 * mm, "offsetDistance" : 25 * mm});
        }
        {
            var Q0;
            Q0=makeQuery(id+"F1.opRevolve","SWEPT_EDGE",EDGE,{"disambiguationData":[OSD([sQuery(id+"F0.wireOp",EDGE,"E0.top"),sQuery(id+"F0.wireOp",EDGE,"E2.trimOffspring")])]});
            var Q1;
            Q1=makeQuery(id+"F1.opRevolve","SWEPT_EDGE",EDGE,{"disambiguationData":[OSD([sQuery(id+"F0.wireOp",EDGE,"E0.bottom"),sQuery(id+"F0.wireOp",EDGE,"E0.right")])]});
            var Q2;
            Q2=makeQuery(id+"F1.opRevolve","SWEPT_EDGE",EDGE,{"disambiguationData":[OSD([sQuery(id+"F0.wireOp",EDGE,"E4.0"),sQuery(id+"F0.wireOp",EDGE,"E4.1")])]});
            var Q3;
            Q3=makeQuery(id+"F1.opRevolve","SWEPT_EDGE",EDGE,{"disambiguationData":[OSD([sQuery(id+"F0.wireOp",EDGE,"E4.1"),sQuery(id+"F0.wireOp",EDGE,"E7")])]});
            fillet(context, id + "F5", {"entities" : qUnion([Q0, Q1, Q2, Q3]), "radius" : 2.5 * mm, "tangentPropagation" : true, "allowEdgeOverflow" : false});
        }
        {
            var Q0;
            Q0=makeQuery(id+"F1.opRevolve","SWEPT_EDGE",EDGE,{"disambiguationData":[OSD([sQuery(id+"F0.wireOp",EDGE,"E5.0"),sQuery(id+"F0.wireOp",EDGE,"E6")])]});
            var Q1;
            Q1=makeQuery(id+"F1.opRevolve","SWEPT_EDGE",EDGE,{"disambiguationData":[OSD([sQuery(id+"F0.wireOp",EDGE,"E4.1"),sQuery(id+"F0.wireOp",EDGE,"E7")])]});
            chamfer(context, id + "F6", {"entities" : qUnion([Q0, Q1]), "width" : 1 * mm, "tangentPropagation" : true});
        }
        {
            var Q0;
            Q0=makeQuery(id+"F1.opRevolve","SWEPT_FACE",FACE,{"disambiguationData":[OSD([sQuery(id+"F0.wireOp",EDGE,"E0.bottom")])]});
            var sketch = newSketch(context, id + "F7", { "sketchPlane" : qUnion([Q0])});
            skCircle(sketch, "E149", {"center": v(0, 0) * mm, "radius": 5 * mm});
            skSolve(sketch);
        }
        {
            var Q0;
            Q0=makeQuery(id+"F7.imprint","IMPRINT",FACE,{"disambiguationData":[TD([[makeQuery(id+"F7.imprint","IMPRINT",EDGE,{"derivedFrom":sQuery(id+"F7.wireOp",EDGE,"E149")}),1.0]])]});
            extrude(context, id + "F8", {"entities" : qUnion([Q0]), "operationType" : NewBodyOperationType.ADD, "oppositeDirection" : true, "depth" : 30 * mm, "offsetDistance" : 25 * mm});
        }
        {
            var Q0;
            Q0=makeQuery(id+"F8.opExtrude","CAP_FACE",FACE,{"disambiguationData":[OSD([sQuery(id+"F7.wireOp",EDGE,"E149")])],"isStart":false});
            var sketch = newSketch(context, id + "F9", { "sketchPlane" : qUnion([Q0])});
            skCircle(sketch, "E150", {"center": v(0, 0) * mm, "radius": 6.5 * mm});
            skSolve(sketch);
        }
        {
            var Q0;
            Q0=makeQuery(id+"F9.imprint","IMPRINT",FACE,{"disambiguationData":[TD([[makeQuery(id+"F9.imprint","IMPRINT",EDGE,{"derivedFrom":sQuery(id+"F9.wireOp",EDGE,"E150")}),1.0]])]});
            var Q1;
            Q1=makeQuery(id+"F9.imprint","IMPRINT",FACE,{"disambiguationData":[TD([[makeQuery(id+"F9.imprint","IMPRINT",EDGE,{"derivedFrom":makeQuery(id+"F8.opExtrude","CAP_EDGE",EDGE,{"disambiguationData":[OSD([sQuery(id+"F7.wireOp",EDGE,"E149")])],"isStart":false})}),-1.0]])]});
            extrude(context, id + "F10", {"entities" : qUnion([Q0, Q1]), "operationType" : NewBodyOperationType.ADD, "depth" : 5 * mm, "offsetDistance" : 25 * mm});
        }
        {
            var Q0;
            Q0=makeQuery(id+"F10.opExtrude","CAP_EDGE",EDGE,{"disambiguationData":[OSD([sQuery(id+"F9.wireOp",EDGE,"E150")])],"isStart":true});
            var Q1;
            Q1=makeQuery(id+"F10.opExtrude","CAP_EDGE",EDGE,{"disambiguationData":[OSD([sQuery(id+"F9.wireOp",EDGE,"E150")])],"isStart":false});
            fillet(context, id + "F11", {"entities" : qUnion([Q0, Q1]), "radius" : 2.5 * mm, "tangentPropagation" : true, "allowEdgeOverflow" : false});
        }
        {
            var Q0;
            Q0=makeQuery(id+"F8.boolean.opBoolean","INTERSECT",EDGE,{"derivedFrom":[makeQuery(id+"F4.boolean.opBoolean","SPLIT",FACE,{"disambiguationData":[TD([makeQuery(id+"F4.opExtrude","SWEPT_FACE",FACE,{"disambiguationData":[OSD([sQuery(id+"F2.wireOp",EDGE,"E9")])]})])],"derivedFrom":makeQuery(id+"F1.opRevolve","SWEPT_FACE",FACE,{"disambiguationData":[OSD([sQuery(id+"F0.wireOp",EDGE,"E0.top")])]})}),makeQuery(id+"F8.opExtrude","SWEPT_FACE",FACE,{"disambiguationData":[OSD([sQuery(id+"F7.wireOp",EDGE,"E149")])]})]});
            fillet(context, id + "F12", {"entities" : qUnion([Q0]), "radius" : 5 * mm, "tangentPropagation" : true, "allowEdgeOverflow" : false});
        }
    });
